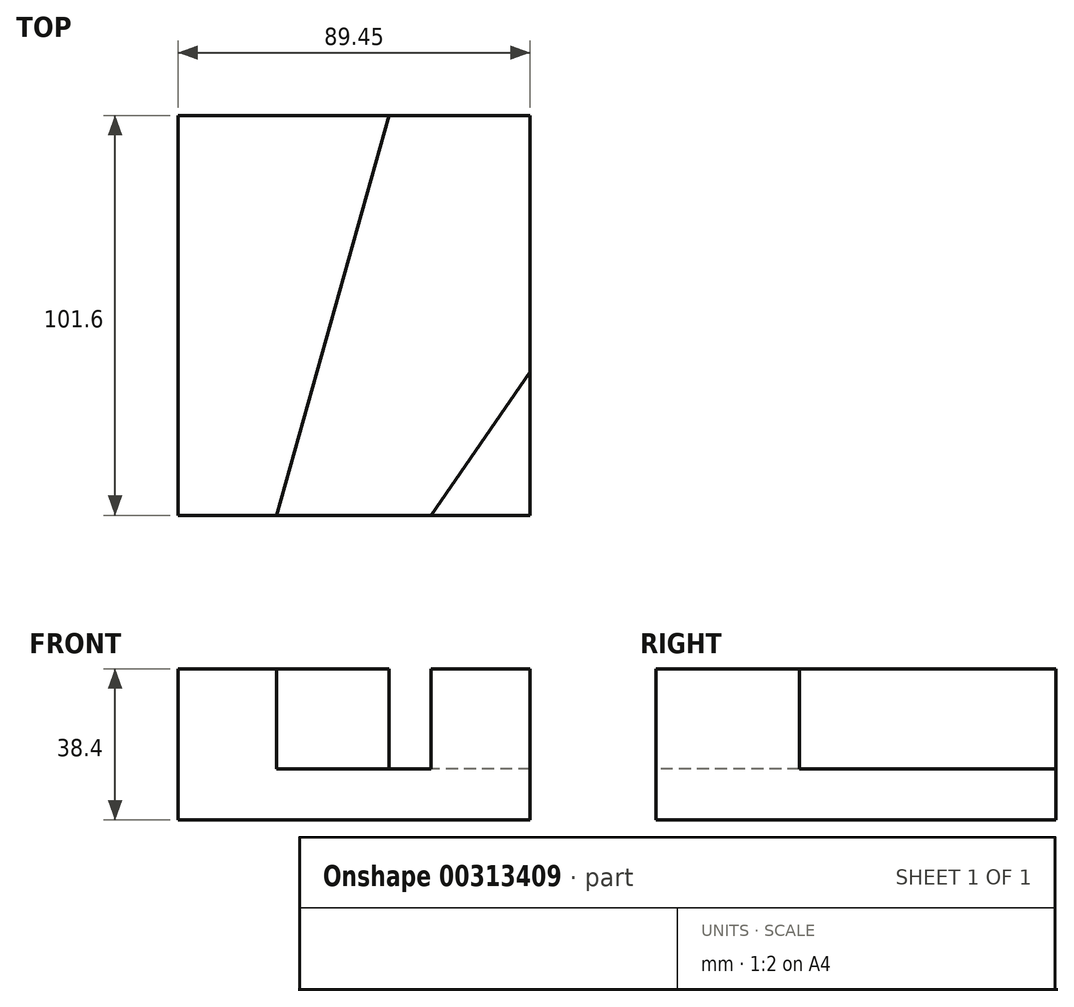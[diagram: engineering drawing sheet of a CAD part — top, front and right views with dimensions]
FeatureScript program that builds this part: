
annotation { "Feature Type Name" : "Feature", "Feature Type Description" : "" }
export const myFeature = defineFeature(function(context is Context, id is Id, definition is map)
    precondition{}
    {
        {
            var Q0;
            Q0=qCreatedBy(makeId("Front.planeOp"),FACE);
            var sketch = newSketch(context, id + "F0", { "sketchPlane" : qUnion([Q0])});
            skLineSegment(sketch, "E0", {"start": v(-53.55, -21.2) * mm, "end": v(-53.55, -34.2) * mm});
            skLineSegment(sketch, "E1", {"start": v(-53.55, -34.2) * mm, "end": v(35.9, -34.2) * mm});
            skLineSegment(sketch, "E2", {"start": v(35.9, -34.2) * mm, "end": v(35.9, -21.2) * mm});
            skLineSegment(sketch, "E3", {"start": v(35.9, -21.2) * mm, "end": v(-53.55, -21.2) * mm});
            skSolve(sketch);
        }
        {
            var Q0;
            Q0 = qSketchRegion(id + "F0", true);
            extrude(context, id + "F1", {"entities" : qUnion([Q0]), "depth" : 25.4 * mm});
        }
        {
            var Q0;
            Q0=makeQuery(id+"F1.opExtrude","CAP_FACE",FACE,{"disambiguationData":[OSD([sQuery(id+"F0.wireOp",EDGE,"E0"),sQuery(id+"F0.wireOp",EDGE,"E1"),sQuery(id+"F0.wireOp",EDGE,"E2"),sQuery(id+"F0.wireOp",EDGE,"E3")])],"isStart":false});
            extrude(context, id + "F2", {"entities" : qUnion([Q0]), "operationType" : NewBodyOperationType.ADD, "depth" : 76.2 * mm});
        }
        {
            var Q0;
            {var subQ0=sQuery(id+"F0.wireOp",EDGE,"E3");Q0=makeQuery(id+"F2.boolean.opBoolean","MERGE",FACE,{"derivedFrom":[makeQuery(id+"F1.opExtrude","SWEPT_FACE",FACE,{"disambiguationData":[OSD([subQ0])]}),makeQuery(id+"F2.opExtrude","SWEPT_FACE",FACE,{"disambiguationData":[OSD([subQ0])]})]});}
            var sketch = newSketch(context, id + "F3", { "sketchPlane" : qUnion([Q0])});
            skLineSegment(sketch, "E4", {"start": v(-53.55, -101.6) * mm, "end": v(-28.5, -101.6) * mm});
            skLineSegment(sketch, "E5", {"start": v(-28.5, -101.6) * mm, "end": v(0, 0) * mm});
            skLineSegment(sketch, "E6", {"start": v(0, 0) * mm, "end": v(-53.55, 0) * mm});
            skLineSegment(sketch, "E7", {"start": v(-53.55, 0) * mm, "end": v(-53.55, -101.6) * mm});
            skSolve(sketch);
        }
        {
            var Q0;
            Q0 = qSketchRegion(id + "F3", true);
            extrude(context, id + "F4", {"entities" : qUnion([Q0]), "operationType" : NewBodyOperationType.ADD, "depth" : 17.78 * mm});
        }
        {
            var Q0;
            Q0=makeQuery(id+"F4.opExtrude","CAP_FACE",FACE,{"disambiguationData":[OSD([sQuery(id+"F3.wireOp",EDGE,"E4"),sQuery(id+"F3.wireOp",EDGE,"E5"),sQuery(id+"F3.wireOp",EDGE,"E6"),sQuery(id+"F3.wireOp",EDGE,"E7")])],"isStart":false});
            extrude(context, id + "F5", {"entities" : qUnion([Q0]), "operationType" : NewBodyOperationType.ADD, "depth" : 7.62 * mm});
        }
        {
            var Q0;
            {var subQ0=sQuery(id+"F0.wireOp",EDGE,"E3");Q0=makeQuery(id+"F2.boolean.opBoolean","MERGE",FACE,{"derivedFrom":[makeQuery(id+"F1.opExtrude","SWEPT_FACE",FACE,{"disambiguationData":[OSD([subQ0])]}),makeQuery(id+"F2.opExtrude","SWEPT_FACE",FACE,{"disambiguationData":[OSD([subQ0])]})]});}
            var sketch = newSketch(context, id + "F6", { "sketchPlane" : qUnion([Q0])});
            skLineSegment(sketch, "E8", {"start": v(10.7, -101.6) * mm, "end": v(35.9, -101.6) * mm});
            skLineSegment(sketch, "E9", {"start": v(35.9, -101.6) * mm, "end": v(35.9, -65.2) * mm});
            skLineSegment(sketch, "E10", {"start": v(35.9, -65.2) * mm, "end": v(10.7, -101.6) * mm});
            skSolve(sketch);
        }
        {
            var Q0;
            Q0 = qSketchRegion(id + "F6", true);
            extrude(context, id + "F7", {"entities" : qUnion([Q0]), "operationType" : NewBodyOperationType.ADD, "depth" : 25.4 * mm});
        }
    });
